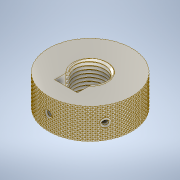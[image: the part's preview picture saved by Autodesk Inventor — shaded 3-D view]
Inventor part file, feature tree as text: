
AUTODESK INVENTOR PART (.ipt)
format: ipt  version: 2020 (Build 240168000, 168)  size: 9,376,768 bytes
history: native  units: in
note: dims shown in document units (in); Inventor stores cm internally (conversion verified against a paired STEP export)
features: sketch x8, helix x3, extrude x2, hole x2, thread x2, revolve x2, pattern_circular x2, plane x1, mirror x1
ambient origin geometry x8: Origin, YZ Plane, XZ Plane, XY Plane, X Axis, Y Axis, Z Axis, Center Point
bodies: Solid1 (feature_tree), Solid2 (feature_tree), Solid3 (feature_tree)
feature tree (23):
  sketch  "Sketch1"  dims[d0=1.375in d1=0.5in d2=0.0in]
  extrude  "Extrusion1"  Depth=0.5in TaperAngle=0.0deg
  hole  "Hole2"  [1 undecoded]
  thread  "Thread1"  [1 undecoded]
  revolve  "Revolution1"  [1 undecoded]
  helix  "Coil1"  [1 undecoded]
  sketch  "Sketch4"  dims[d29=0.0556in d30=0.6111in d31=0.3937in d32=0.0in d33=0.0in d34=0.0in d35=0.0in d36=0.0in d37=0.1875in d38=0.1875in]
  plane  "Work Plane1"
  hole  "Hole3"  [1 undecoded]
  thread  "Thread2"  [1 undecoded]
  revolve  "Revolution2"  Angle=30.0deg
  helix  "Coil2"  [1 undecoded]
  pattern_circular  "Circular Pattern1"  [2 undecoded]
  extrude  "Extrusion3"  Depth=0.3779in
  helix  "Coil3"  [1 undecoded]
  pattern_circular  "Circular Pattern2"  Count=3 Angle=120.0deg
  mirror  "Mirror1"
  sketch  "Sketch2"  dims[d10=0.565in d11=1.25in d12=0.375in d13=0.25in d14=0.5635in d15=1.0in d16=0.0in d17=0.5in d18=0.0in d19=0.3779in d20=0.0089in d21=0.0089in]
  sketch  "Sketch3"  dims[d24=0.0556in d26=0.3779in d28=0.0in]
  sketch  "Sketch5"  dims[d39=0.3059in d42=30.0deg d43=0.25in]
  sketch  "Sketch6"  dims[d44=0.145in d45=0.38in d46=0.375in d47=0.25in d48=0.5635in d49=0.588in d50=0.0in]
  sketch  "Sketch7"  dims[d51=0.414in d52=0.0in]
  sketch  "Sketch8"  dims[d53=0.3779in d54=0.0067in d55=0.0067in d58=0.0417in d60=0.3779in d62=0.0in d63=0.0417in d64=0.4978in d65=0.3937in d66=0.0in d67=0.0in d68=0.0in d69=0.0in d70=0.0in d71=1.1811in d72=120.0deg d74=0.0in d75=0.0in d76=0.0172in d77=0.0305in d78=1.0in d79=0.5in d80=0.0492in d81=0.0in d82=90.0deg d83=90.0deg d84=0.0in d85=0.0in d86=28.3465in d87=360.0deg]
note: 10 required parameter values undecoded (feature->parameter linkage not recoverable at this tier; creation-order binding heuristic only, values carry confidence <= 0.55)